# Revit family: Haworth_BuzziDonut
name_source: partatom
category: Furniture
revit_build: Autodesk Revit 2018 (Build: 20170223_1515(x64)
units: mm (PartAtom-declared; Revit-internal decimal feet)

## family parameters
Cut with Voids When Loaded = No
Host = Face
Room Calculation Point = No
Shared = No

## types (3) — shared parameters
3D Drop = Yes
3D Leaf = No
3D Rib = No
Actual Height = 2.36 "
Assembly Code = E2020200
Flat = No
Manufacturer = Haworth
Model = HCBZ-DNS
Note = Verify Final Dim. w/ Haworth
Trim Finish = Haworth _ Paint _ Black
URL = https://www.haworth.com
URL - Product = https://www.haworth.com
Warranty = https://www.haworth.com
zero-valued in all types: Default Elevation

## per-type parameters (varying)
| type | Actual Depth | Actual Width | Description | Large | Medium | Small |
| HCBZ-DNS3 - Large | 47.24 " | 47.24 " | Haworth BuzziDonut Large | Yes | No | No |
| HCBZ-DNS2 - Medium | 39.37 " | 39.37 " | Haworth BuzziDonut Medium | No | Yes | No |
| HCBZ-DNS1 - Small | 31.5 " | 31.5 " | Haworth BuzziDonut Small | No | No | Yes |

## geometry (parser evidence)
native form markers: Sweep x11
no freeform markers — native parametric forms only
